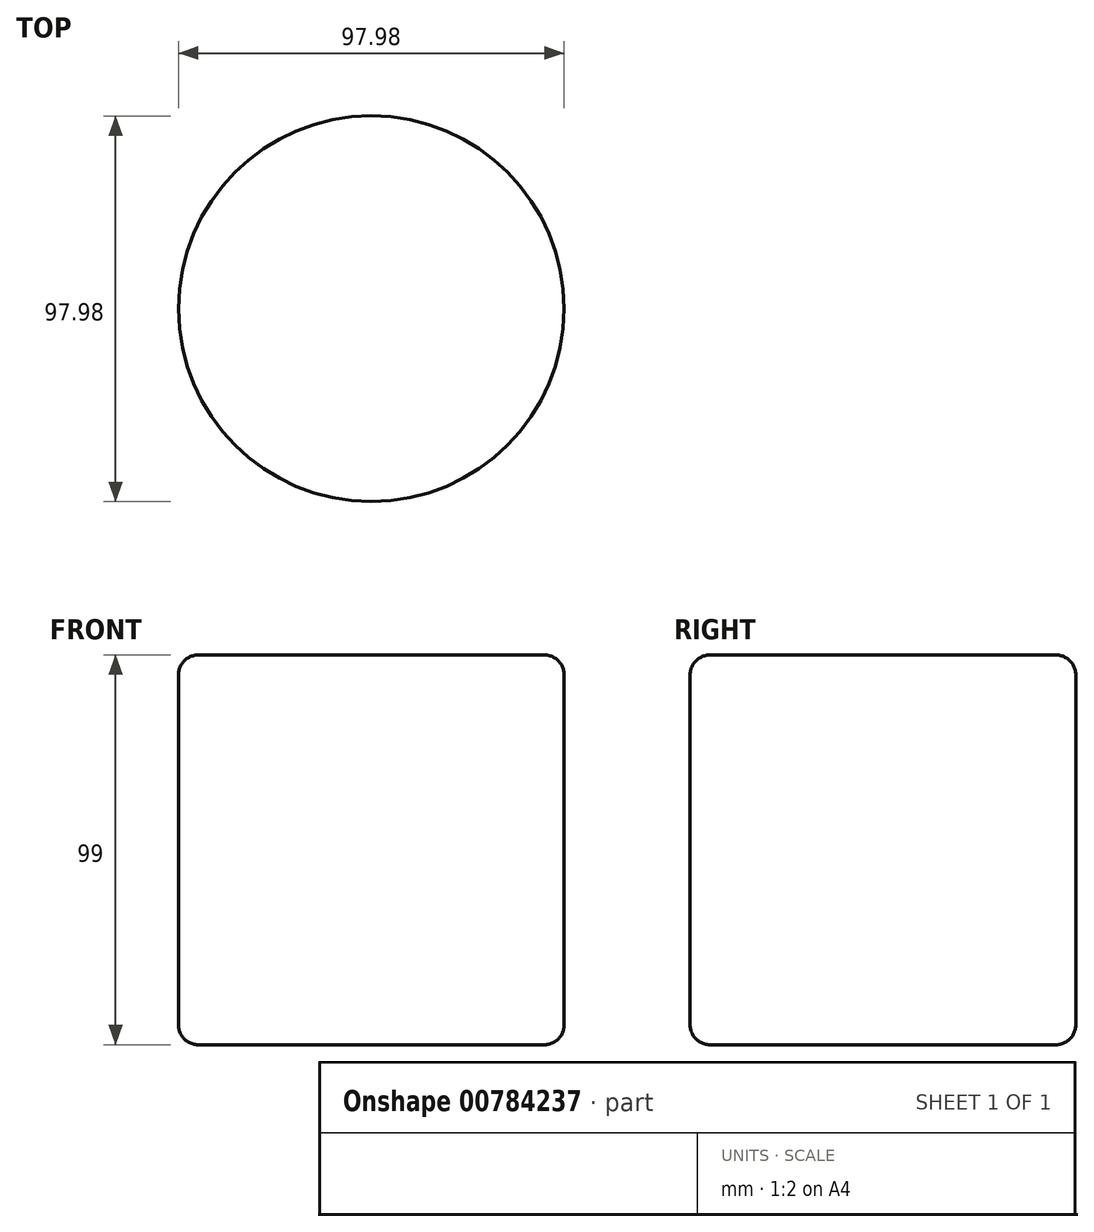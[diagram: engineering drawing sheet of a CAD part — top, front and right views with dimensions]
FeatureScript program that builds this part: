
annotation { "Feature Type Name" : "Feature", "Feature Type Description" : "" }
export const myFeature = defineFeature(function(context is Context, id is Id, definition is map)
    precondition{}
    {
        {
            var Q0;
            Q0=qCreatedBy(makeId("Top.planeOp"),FACE);
            var sketch = newSketch(context, id + "F0", { "sketchPlane" : qUnion([Q0])});
            skCircle(sketch, "E0", {"center": v(90.13, 19.11) * mm, "radius": 48.99 * mm});
            skSolve(sketch);
        }
        {
            var Q0;
            Q0=qSketchRegion(id+"F0",true);
            extrude(context, id + "F1", {"entities" : qUnion([Q0]), "depth" : 99 * mm});
        }
        {
            var Q0;
            Q0=makeQuery(id+"F1.opExtrude","CAP_EDGE",EDGE,{"disambiguationData":[OSD([sQuery(id+"F0.wireOp",EDGE,"E0")])],"isStart":true});
            fillet(context, id + "F2", {"entities" : qUnion([Q0]), "radius" : 5 * mm, "tangentPropagation" : true, "allowEdgeOverflow" : false});
        }
        {
            var Q0;
            Q0=makeQuery(id+"F1.opExtrude","CAP_EDGE",EDGE,{"disambiguationData":[OSD([sQuery(id+"F0.wireOp",EDGE,"E0")])],"isStart":false});
            fillet(context, id + "F3", {"entities" : qUnion([Q0]), "radius" : 5 * mm, "tangentPropagation" : true, "allowEdgeOverflow" : false});
        }
    });
